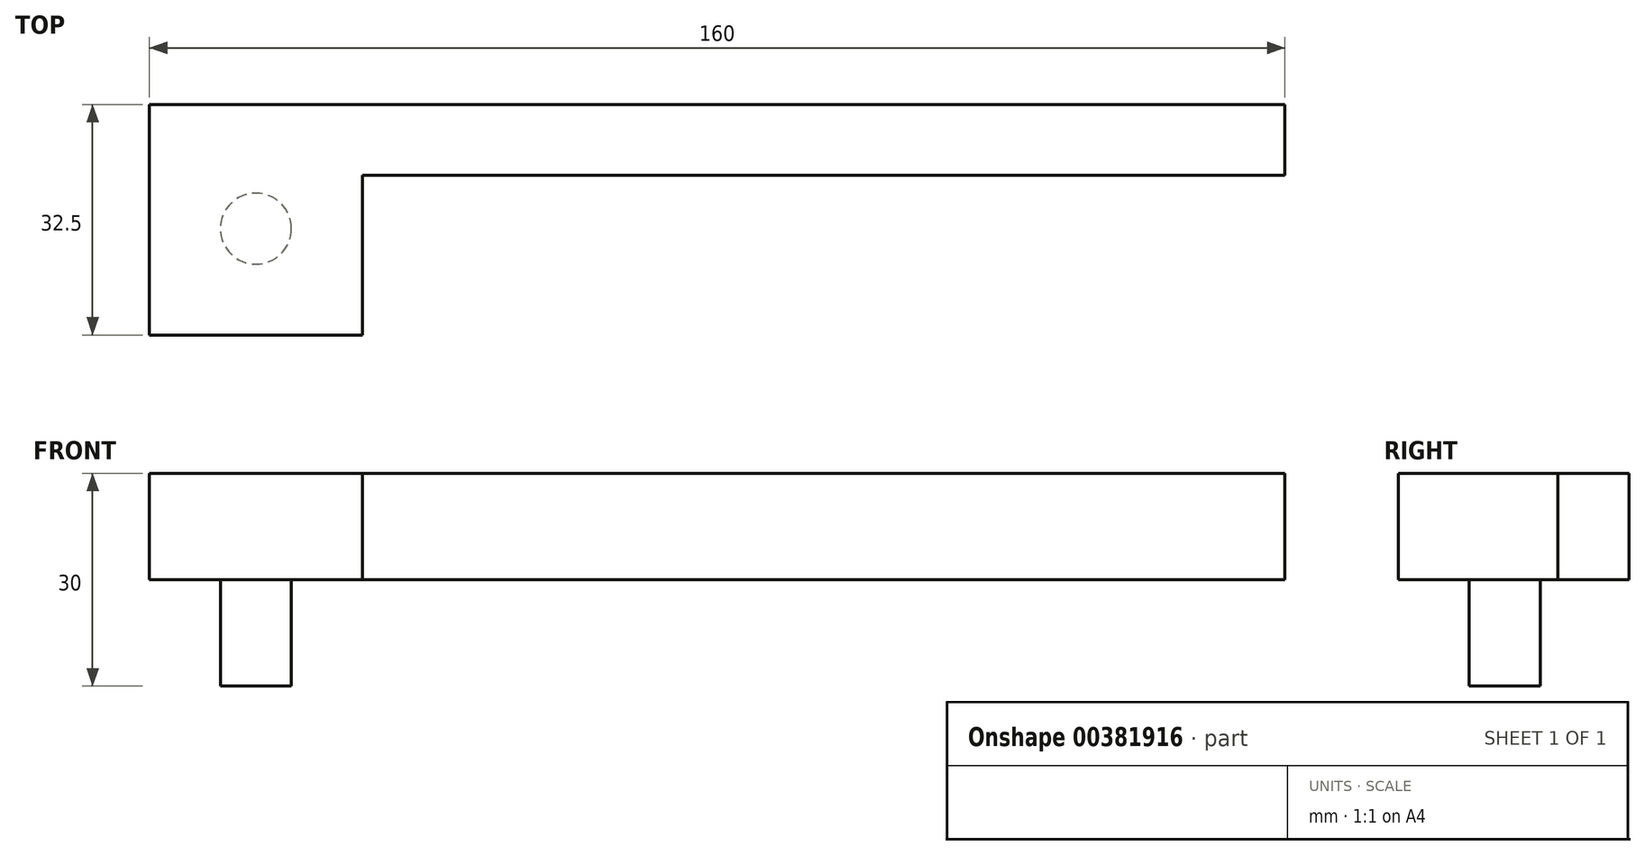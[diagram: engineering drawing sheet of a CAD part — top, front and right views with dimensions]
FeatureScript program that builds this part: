
annotation { "Feature Type Name" : "Feature", "Feature Type Description" : "" }
export const myFeature = defineFeature(function(context is Context, id is Id, definition is map)
    precondition{}
    {
        {
            var Q0;
            Q0=qCreatedBy(makeId("Top.planeOp"),FACE);
            var sketch = newSketch(context, id + "F0", { "sketchPlane" : qUnion([Q0])});
            skLineSegment(sketch, "E0.bottom", {"start": v(0, 0) * mm, "end": v(160, 0) * mm, "construction": true});
            skLineSegment(sketch, "E0.top", {"start": v(0, 80) * mm, "end": v(160, 80) * mm, "construction": true});
            skLineSegment(sketch, "E0.left", {"start": v(0, 0) * mm, "end": v(0, 80) * mm, "construction": true});
            skLineSegment(sketch, "E0.right", {"start": v(160, 0) * mm, "end": v(160, 80) * mm, "construction": true});
            skArc(sketch, "E1", {"start": v(15, 20) * mm, "mid": v(10, 15) * mm, "end": v(15, 10) * mm, "construction": true});
            skLineSegment(sketch, "E2", {"start": v(0, 15) * mm, "end": v(160, 15) * mm, "construction": true});
            skArc(sketch, "E3", {"start": v(145, 10) * mm, "mid": v(150, 15) * mm, "end": v(145, 20) * mm, "construction": true});
            skLineSegment(sketch, "E4", {"start": v(15, 20) * mm, "end": v(145, 20) * mm, "construction": true});
            skLineSegment(sketch, "E5", {"start": v(145, 10) * mm, "end": v(15, 10) * mm, "construction": true});
            skCircle(sketch, "E6", {"center": v(130, 50) * mm, "radius": 4 * mm, "construction": true});
            skCircle(sketch, "E7", {"center": v(130, 50) * mm, "radius": 17.5 * mm, "construction": true});
            skCircle(sketch, "E8", {"center": v(117, 50) * mm, "radius": 2.5 * mm, "construction": true});
            skArc(sketch, "E9", {"start": v(20, 55) * mm, "mid": v(15, 50) * mm, "end": v(20, 45) * mm, "construction": true});
            skArc(sketch, "E10", {"start": v(46, 45) * mm, "mid": v(51, 50) * mm, "end": v(46, 55) * mm, "construction": true});
            skLineSegment(sketch, "E11", {"start": v(20, 50) * mm, "end": v(46, 50) * mm, "construction": true});
            skLineSegment(sketch, "E12", {"start": v(20, 55) * mm, "end": v(46, 55) * mm, "construction": true});
            skLineSegment(sketch, "E13", {"start": v(20, 45) * mm, "end": v(46, 45) * mm, "construction": true});
            skLineSegment(sketch, "E14.bottom", {"start": v(0, 0) * mm, "end": v(30, 0) * mm});
            skLineSegment(sketch, "E14.top", {"start": v(0, 32.5) * mm, "end": v(30, 32.5) * mm});
            skLineSegment(sketch, "E14.left", {"start": v(0, 0) * mm, "end": v(0, 32.5) * mm});
            skLineSegment(sketch, "E14.right", {"start": v(30, 0) * mm, "end": v(30, 32.5) * mm});
            skCircle(sketch, "E15", {"center": v(15, 15) * mm, "radius": 5 * mm});
            skLineSegment(sketch, "E16", {"start": v(30, 32.5) * mm, "end": v(160, 32.5) * mm});
            skLineSegment(sketch, "E17", {"start": v(160, 32.5) * mm, "end": v(160, 22.5) * mm});
            skLineSegment(sketch, "E18", {"start": v(160, 22.5) * mm, "end": v(30, 22.5) * mm});
            skSolve(sketch);
        }
        {
            var Q0;
            {var subQ1=sQuery(id+"F0.wireOp",EDGE,"E14.bottom");Q0=makeQuery(id+"F0.imprint","IMPRINT",FACE,{"disambiguationData":[TD([[makeQuery(id+"F0.imprint","IMPRINT",EDGE,{"derivedFrom":subQ1}),1.0]])]});}
            var Q1;
            {var subQ0=sQuery(id+"F0.wireOp",EDGE,"E16");Q1=makeQuery(id+"F0.imprint","IMPRINT",FACE,{"disambiguationData":[TD([[makeQuery(id+"F0.imprint","IMPRINT",EDGE,{"derivedFrom":subQ0}),-1.0]])]});}
            var Q2;
            Q2=makeQuery(id+"F0.imprint","IMPRINT",FACE,{"disambiguationData":[TD([[makeQuery(id+"F0.imprint","IMPRINT",EDGE,{"derivedFrom":sQuery(id+"F0.wireOp",EDGE,"E15")}),1.0]])]});
            extrude(context, id + "F1", {"entities" : qUnion([Q0, Q1, Q2]), "depth" : (15) * mm});
        }
        {
            var Q0;
            Q0=makeQuery(id+"F0.imprint","IMPRINT",FACE,{"disambiguationData":[TD([[makeQuery(id+"F0.imprint","IMPRINT",EDGE,{"derivedFrom":sQuery(id+"F0.wireOp",EDGE,"E15")}),1.0]])]});
            extrude(context, id + "F2", {"entities" : qUnion([Q0]), "operationType" : NewBodyOperationType.ADD, "oppositeDirection" : true, "depth" : (15) * mm});
        }
    });
